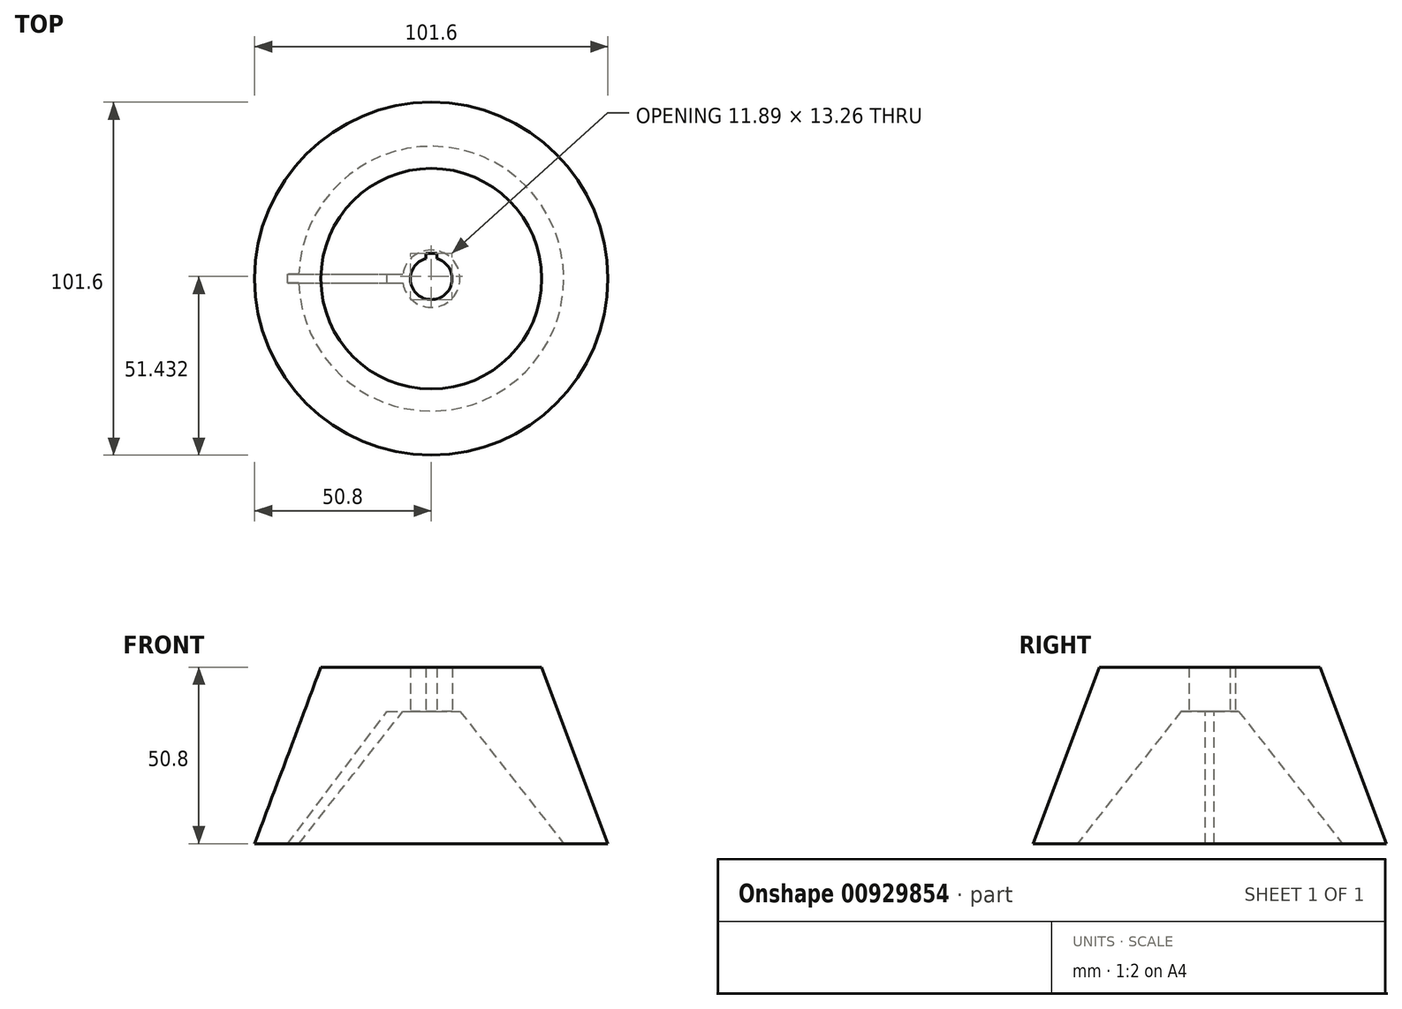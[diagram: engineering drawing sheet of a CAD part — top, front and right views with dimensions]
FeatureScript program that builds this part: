
annotation { "Feature Type Name" : "Feature", "Feature Type Description" : "" }
export const myFeature = defineFeature(function(context is Context, id is Id, definition is map)
    precondition{}
    {
        {
            var Q0;
            Q0=qCreatedBy(makeId("Front.planeOp"),FACE);
            var sketch = newSketch(context, id + "F0", { "sketchPlane" : qUnion([Q0])});
            skLineSegment(sketch, "E0.bottom", {"start": v(0, 0) * mm, "end": v(-50.8, 0) * mm});
            skLineSegment(sketch, "E0.top", {"start": v(0, 50.8) * mm, "end": v(-31.75, 50.8) * mm});
            skLineSegment(sketch, "E0.left", {"start": v(0, 0) * mm, "end": v(0, 50.8) * mm});
            skLineSegment(sketch, "E0.right", {"start": v(-50.8, 0) * mm, "end": v(-31.75, 50.8) * mm});
            skLineSegment(sketch, "E1.bottom", {"start": v(0, 50.8) * mm, "end": v(-12.7, 50.8) * mm});
            skLineSegment(sketch, "E1.top", {"start": v(0, 63.5) * mm, "end": v(-12.7, 63.5) * mm});
            skLineSegment(sketch, "E1.left", {"start": v(0, 50.8) * mm, "end": v(0, 63.5) * mm});
            skLineSegment(sketch, "E1.right", {"start": v(-12.7, 50.8) * mm, "end": v(-12.7, 63.5) * mm});
            skSolve(sketch);
        }
        {
            var Q0;
            Q0=makeQuery(id+"F0.imprint","IMPRINT",FACE,{"disambiguationData":[TD([[makeQuery(id+"F0.imprint","IMPRINT",EDGE,{"derivedFrom":sQuery(id+"F0.wireOp",EDGE,"E0.bottom")}),-1.0]])]});
            var Q1;
            Q1=makeQuery(id+"F0.imprint","IMPRINT",FACE,{"disambiguationData":[TD([[makeQuery(id+"F0.imprint","IMPRINT",EDGE,{"derivedFrom":sQuery(id+"F0.wireOp",EDGE,"E1.bottom")}),-1.0]])]});
            var Q2;
            Q2=sQuery(id+"F0.wireOp",EDGE,"E0.left");
            revolve(context, id + "F1", {"surfaceOperationType" : NewSurfaceOperationType.NEW, "entities" : qUnion([Q0, Q1]), "axis" : qUnion([Q2]), "revolveType" : RevolveType.FULL});
        }
        {
            var Q0;
            Q0=qCreatedBy(makeId("Front.planeOp"),FACE);
            var sketch = newSketch(context, id + "F2", { "sketchPlane" : qUnion([Q0])});
            skLineSegment(sketch, "E2", {"start": v(-38.1, 0) * mm, "end": v(-8.25, 38.1) * mm});
            skLineSegment(sketch, "E3", {"start": v(-8.26, 38.1) * mm, "end": v(0, 38.1) * mm});
            skLineSegment(sketch, "E4", {"start": v(0, 38.1) * mm, "end": v(0, 0) * mm});
            skLineSegment(sketch, "E5", {"start": v(0, 0) * mm, "end": v(-38.1, 0) * mm});
            skLineSegment(sketch, "E6", {"start": v(0, 38.1) * mm, "end": v(0, 63.5) * mm});
            skLineSegment(sketch, "E7", {"start": v(0, 63.5) * mm, "end": v(-6, 63.5) * mm});
            skLineSegment(sketch, "E8", {"start": v(-6, 63.5) * mm, "end": v(-6, 38.1) * mm});
            skSolve(sketch);
        }
        {
            var Q0;
            Q0 = qSketchRegion(id + "F2", true);
            var Q1;
            Q1=sQuery(id+"F2.wireOp",EDGE,"E4");
            revolve(context, id + "F3", {"operationType" : NewBodyOperationType.REMOVE, "surfaceOperationType" : NewSurfaceOperationType.NEW, "entities" : qUnion([Q0]), "axis" : qUnion([Q1]), "revolveType" : RevolveType.FULL, "oppositeDirection" : true});
        }
        {
            var Q0;
            Q0=qCreatedBy(makeId("Top.planeOp"),FACE);
            var sketch = newSketch(context, id + "F4", { "sketchPlane" : qUnion([Q0])});
            skLineSegment(sketch, "E9.bottom", {"start": v(1.59, 0) * mm, "end": v(-1.59, 0) * mm});
            skLineSegment(sketch, "E9.top", {"start": v(1.59, 7.26) * mm, "end": v(-1.59, 7.26) * mm});
            skLineSegment(sketch, "E9.left", {"start": v(1.59, 0) * mm, "end": v(1.59, 7.26) * mm});
            skLineSegment(sketch, "E9.right", {"start": v(-1.59, 0) * mm, "end": v(-1.59, 7.26) * mm});
            skSolve(sketch);
        }
        {
            var Q0;
            Q0=makeQuery(id+"F4.imprint","IMPRINT",FACE,{"disambiguationData":[TD([[makeQuery(id+"F4.imprint","IMPRINT",EDGE,{"derivedFrom":sQuery(id+"F4.wireOp",EDGE,"E9.bottom")}),-1.0]])]});
            extrude(context, id + "F5", {"entities" : qUnion([Q0]), "operationType" : NewBodyOperationType.REMOVE, "endBound" : BoundingType.THROUGH_ALL, "depth" : 25.4 * mm, "offsetDistance" : 25.4 * mm});
        }
        {
            var Q0;
            Q0=qCreatedBy(makeId("Front.planeOp"),FACE);
            var sketch = newSketch(context, id + "F6", { "sketchPlane" : qUnion([Q0])});
            skLineSegment(sketch, "E10", {"start": v(-41.28, 0) * mm, "end": v(-12.7, 38.1) * mm});
            skLineSegment(sketch, "E11", {"start": v(-12.7, 38.1) * mm, "end": v(-6.35, 38.1) * mm});
            skLineSegment(sketch, "E12", {"start": v(-6.35, 38.1) * mm, "end": v(-34.92, 0) * mm});
            skLineSegment(sketch, "E13", {"start": v(-34.92, 0) * mm, "end": v(-41.28, 0) * mm});
            skPoint(sketch, "E14", {"position": v(-38.1, 0) * mm});
            skPoint(sketch, "E15", {"position": v(-9.53, 38.1) * mm});
            skSolve(sketch);
        }
        {
            var Q0;
            Q0=makeQuery(id+"F6.imprint","IMPRINT",FACE,{"disambiguationData":[TD([[makeQuery(id+"F6.imprint","IMPRINT",EDGE,{"derivedFrom":sQuery(id+"F6.wireOp",EDGE,"E10")}),-1.0]])]});
            extrude(context, id + "F7", {"entities" : qUnion([Q0]), "operationType" : NewBodyOperationType.REMOVE, "endBound" : BoundingType.SYMMETRIC, "depth" : 2.54 * mm, "offsetDistance" : 25.4 * mm});
        }
    });
